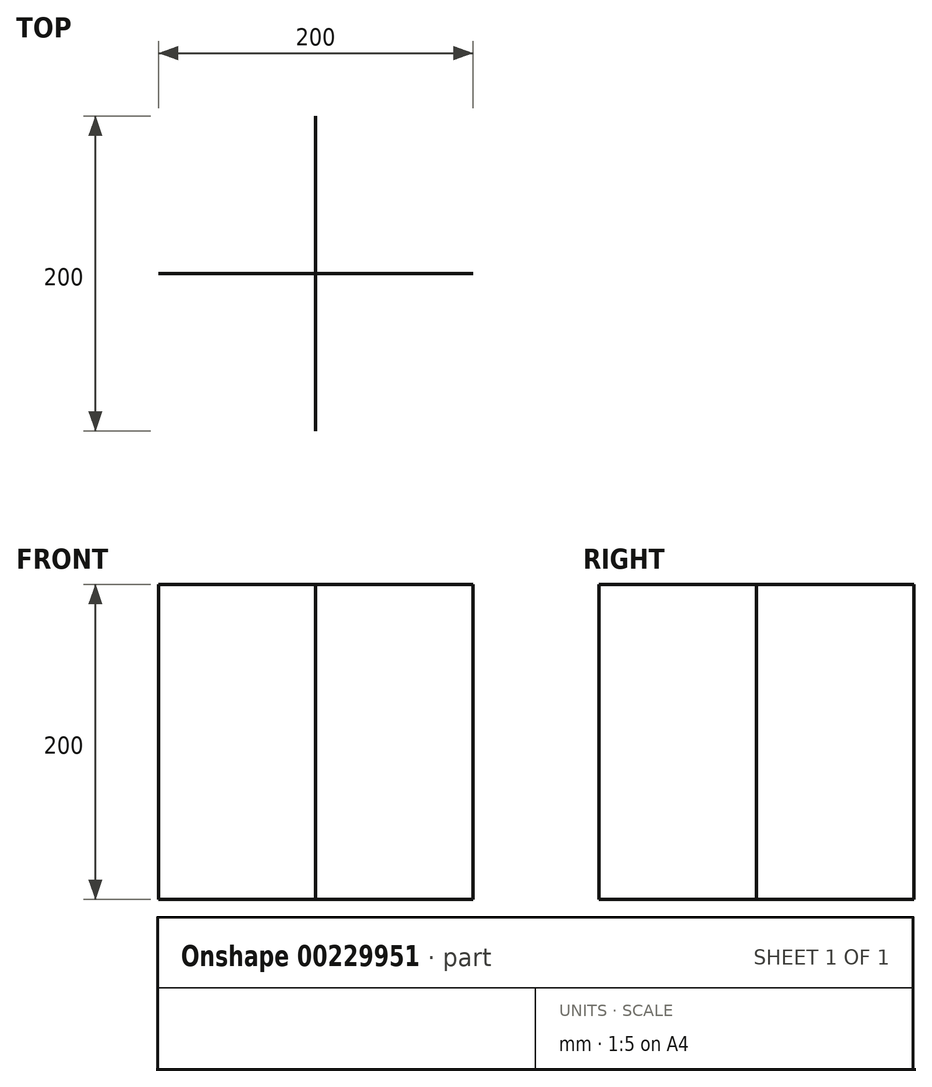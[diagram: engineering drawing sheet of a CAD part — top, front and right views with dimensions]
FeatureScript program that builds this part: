
annotation { "Feature Type Name" : "Feature", "Feature Type Description" : "" }
export const myFeature = defineFeature(function(context is Context, id is Id, definition is map)
    precondition{}
    {
        {
            var Q0;
            Q0=qCreatedBy(makeId("Top.planeOp"),FACE);
            var sketch = newSketch(context, id + "F0", { "sketchPlane" : qUnion([Q0])});
            skLineSegment(sketch, "E0", {"start": v(0, 100) * mm, "end": v(0, -100) * mm});
            skSolve(sketch);
        }
        {
            var Q0;
            Q0=qCreatedBy(makeId("Top.planeOp"),FACE);
            var sketch = newSketch(context, id + "F1", { "sketchPlane" : qUnion([Q0])});
            skLineSegment(sketch, "E1", {"start": v(-100, 0) * mm, "end": v(100, 0) * mm});
            skSolve(sketch);
        }
        {
            var Q0;
            Q0 = qBodyType(qCreatedBy(id + "F0" ,EDGE), BodyType.WIRE);
            extrude(context, id + "F2", {"bodyType" : ToolBodyType.SURFACE, "surfaceEntities" : qUnion([Q0]), "depth" : 100 * mm, "hasSecondDirection" : true, "secondDirectionOppositeDirection" : true, "secondDirectionDepth" : 100 * mm});
        }
        {
            var Q0;
            Q0 = qBodyType(qCreatedBy(id + "F1" ,EDGE), BodyType.WIRE);
            extrude(context, id + "F3", {"bodyType" : ToolBodyType.SURFACE, "surfaceEntities" : qUnion([Q0]), "depth" : 100 * mm, "hasSecondDirection" : true, "secondDirectionOppositeDirection" : true, "secondDirectionDepth" : 100 * mm});
        }
        {
            var Q0;
            Q0=qCreatedBy(makeId("Top.planeOp"),FACE);
            var sketch = newSketch(context, id + "F4", { "sketchPlane" : qUnion([Q0])});
            skLineSegment(sketch, "E2", {"start": v(-100, -100) * mm, "end": v(100, -100) * mm});
            skLineSegment(sketch, "E3", {"start": v(0, 100) * mm, "end": v(0, -100) * mm});
            skSolve(sketch);
        }
    });
